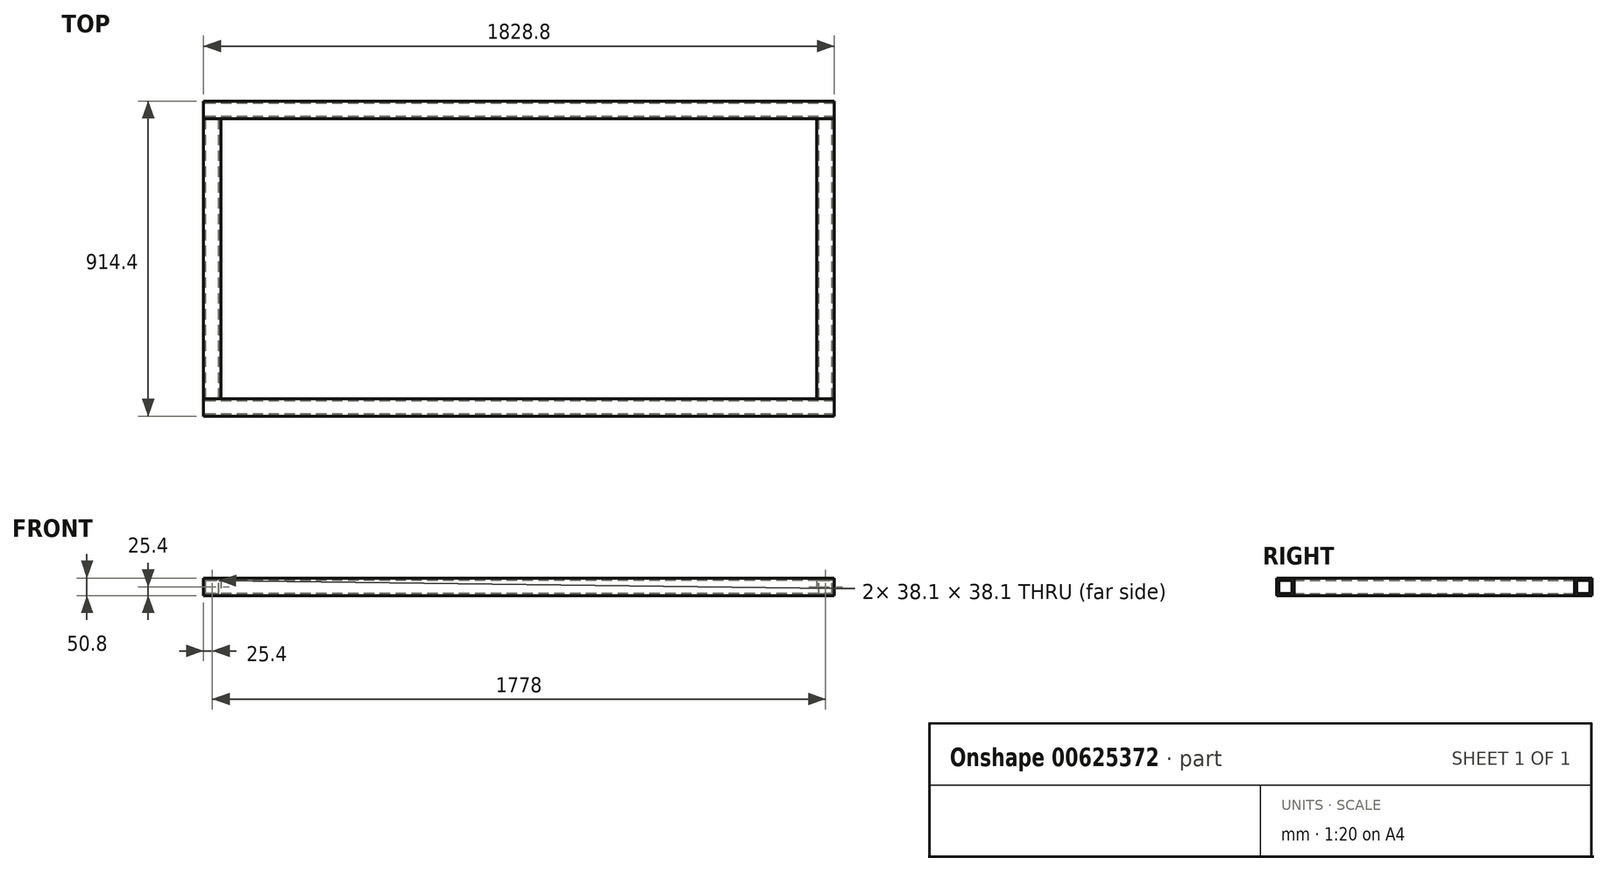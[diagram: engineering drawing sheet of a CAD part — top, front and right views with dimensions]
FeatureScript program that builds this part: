
annotation { "Feature Type Name" : "Feature", "Feature Type Description" : "" }
export const myFeature = defineFeature(function(context is Context, id is Id, definition is map)
    precondition{}
    {
        {
            var Q0;
            Q0=qCreatedBy(makeId("Front.planeOp"),FACE);
            var sketch = newSketch(context, id + "F0", { "sketchPlane" : qUnion([Q0])});
            skLineSegment(sketch, "E0.bottom", {"start": v(-25.4, 25.4) * mm, "end": v(25.4, 25.4) * mm});
            skLineSegment(sketch, "E0.top", {"start": v(-25.4, -25.4) * mm, "end": v(25.4, -25.4) * mm});
            skLineSegment(sketch, "E0.left", {"start": v(-25.4, 25.4) * mm, "end": v(-25.4, -25.4) * mm});
            skLineSegment(sketch, "E0.right", {"start": v(25.4, 25.4) * mm, "end": v(25.4, -25.4) * mm});
            skPoint(sketch, "E0.middle", {"position": v(0, 0) * mm});
            skLineSegment(sketch, "E1.bottom", {"start": v(-19.05, -19.05) * mm, "end": v(19.05, -19.05) * mm});
            skLineSegment(sketch, "E1.top", {"start": v(-19.05, 19.05) * mm, "end": v(19.05, 19.05) * mm});
            skLineSegment(sketch, "E1.left", {"start": v(-19.05, -19.05) * mm, "end": v(-19.05, 19.05) * mm});
            skLineSegment(sketch, "E1.right", {"start": v(19.05, -19.05) * mm, "end": v(19.05, 19.05) * mm});
            skSolve(sketch);
        }
        {
            var Q0;
            Q0=makeQuery(id+"F0.imprint","IMPRINT",FACE,{"disambiguationData":[TD([[makeQuery(id+"F0.imprint","IMPRINT",EDGE,{"derivedFrom":sQuery(id+"F0.wireOp",EDGE,"E0.bottom")}),-1.0]])]});
            extrude(context, id + "F1", {"entities" : qUnion([Q0]), "depth" : 812.8 * mm, "offsetDistance" : 25.4 * mm});
        }
        {
            var Q0;
            Q0=qCreatedBy(makeId("Right.planeOp"),FACE);
            var sketch = newSketch(context, id + "F2", { "sketchPlane" : qUnion([Q0])});
            skLineSegment(sketch, "E2.bottom", {"start": v(76.2, 25.4) * mm, "end": v(25.4, 25.4) * mm});
            skLineSegment(sketch, "E2.top", {"start": v(76.2, -25.4) * mm, "end": v(25.4, -25.4) * mm});
            skLineSegment(sketch, "E2.left", {"start": v(76.2, 25.4) * mm, "end": v(76.2, -25.4) * mm});
            skLineSegment(sketch, "E2.right", {"start": v(25.4, 25.4) * mm, "end": v(25.4, -25.4) * mm});
            skPoint(sketch, "E2.middle", {"position": v(50.8, 0) * mm});
            skLineSegment(sketch, "E3.bottom", {"start": v(69.85, 19.05) * mm, "end": v(31.75, 19.05) * mm});
            skLineSegment(sketch, "E3.top", {"start": v(69.85, -19.05) * mm, "end": v(31.75, -19.05) * mm});
            skLineSegment(sketch, "E3.left", {"start": v(69.85, 19.05) * mm, "end": v(69.85, -19.05) * mm});
            skLineSegment(sketch, "E3.right", {"start": v(31.75, 19.05) * mm, "end": v(31.75, -19.05) * mm});
            skSolve(sketch);
        }
        {
            var Q0;
            Q0=makeQuery(id+"F2.imprint","IMPRINT",FACE,{"disambiguationData":[TD([[makeQuery(id+"F2.imprint","IMPRINT",EDGE,{"derivedFrom":sQuery(id+"F2.wireOp",EDGE,"E2.bottom")}),1.0]])]});
            extrude(context, id + "F3", {"entities" : qUnion([Q0]), "depth" : 1828.8 * mm, "offsetDistance" : 25.4 * mm});
        }
        {
            var Q0;
            Q0=makeQuery(id+"F3.opExtrude","SWEPT_BODY",BODY,{"disambiguationData":[OSD([sQuery(id+"F2.wireOp",EDGE,"E2.bottom"),sQuery(id+"F2.wireOp",EDGE,"E2.top"),sQuery(id+"F2.wireOp",EDGE,"E2.left"),sQuery(id+"F2.wireOp",EDGE,"E2.right"),sQuery(id+"F2.wireOp",EDGE,"E3.bottom"),sQuery(id+"F2.wireOp",EDGE,"E3.top"),sQuery(id+"F2.wireOp",EDGE,"E3.left"),sQuery(id+"F2.wireOp",EDGE,"E3.right")])]});
            var Q1;
            Q1=qCreatedBy(makeId("Front.planeOp"),FACE);
            transform(context, id + "F4", {"entities" : qUnion([Q0]), "transformType" : TransformType.TRANSLATION_DISTANCE, "transformDirection" : qUnion([Q1]), "distance" : 25.4 * mm, "makeCopy" : false});
        }
        {
            var Q0;
            Q0=makeQuery(id+"F3.opExtrude","SWEPT_BODY",BODY,{"disambiguationData":[OSD([sQuery(id+"F2.wireOp",EDGE,"E2.bottom"),sQuery(id+"F2.wireOp",EDGE,"E2.top"),sQuery(id+"F2.wireOp",EDGE,"E2.left"),sQuery(id+"F2.wireOp",EDGE,"E2.right"),sQuery(id+"F2.wireOp",EDGE,"E3.bottom"),sQuery(id+"F2.wireOp",EDGE,"E3.top"),sQuery(id+"F2.wireOp",EDGE,"E3.left"),sQuery(id+"F2.wireOp",EDGE,"E3.right")])]});
            var Q1;
            Q1=qCreatedBy(makeId("Right.planeOp"),FACE);
            transform(context, id + "F5", {"entities" : qUnion([Q0]), "transformType" : TransformType.TRANSLATION_DISTANCE, "transformDirection" : qUnion([Q1]), "distance" : 25.4 * mm, "oppositeDirection" : true, "makeCopy" : false});
        }
        {
            var Q0;
            Q0=makeQuery(id+"F3.opExtrude","SWEPT_BODY",BODY,{"disambiguationData":[OSD([sQuery(id+"F2.wireOp",EDGE,"E2.bottom"),sQuery(id+"F2.wireOp",EDGE,"E2.top"),sQuery(id+"F2.wireOp",EDGE,"E2.left"),sQuery(id+"F2.wireOp",EDGE,"E2.right"),sQuery(id+"F2.wireOp",EDGE,"E3.bottom"),sQuery(id+"F2.wireOp",EDGE,"E3.top"),sQuery(id+"F2.wireOp",EDGE,"E3.left"),sQuery(id+"F2.wireOp",EDGE,"E3.right")])]});
            var Q1;
            Q1=qCreatedBy(makeId("Front.planeOp"),FACE);
            transform(context, id + "F6", {"entities" : qUnion([Q0]), "transformType" : TransformType.TRANSLATION_DISTANCE, "transformDirection" : qUnion([Q1]), "distance" : 863.6 * mm, "makeCopy" : true});
        }
        {
            var Q0;
            Q0=makeQuery(id+"F1.opExtrude","SWEPT_BODY",BODY,{"disambiguationData":[OSD([sQuery(id+"F0.wireOp",EDGE,"E0.bottom"),sQuery(id+"F0.wireOp",EDGE,"E0.top"),sQuery(id+"F0.wireOp",EDGE,"E0.left"),sQuery(id+"F0.wireOp",EDGE,"E0.right"),sQuery(id+"F0.wireOp",EDGE,"E1.bottom"),sQuery(id+"F0.wireOp",EDGE,"E1.top"),sQuery(id+"F0.wireOp",EDGE,"E1.left"),sQuery(id+"F0.wireOp",EDGE,"E1.right")])]});
            var Q1;
            Q1=qCreatedBy(makeId("Right.planeOp"),FACE);
            transform(context, id + "F7", {"entities" : qUnion([Q0]), "transformType" : TransformType.TRANSLATION_DISTANCE, "transformDirection" : qUnion([Q1]), "distance" : 1778 * mm, "makeCopy" : true});
        }
    });
